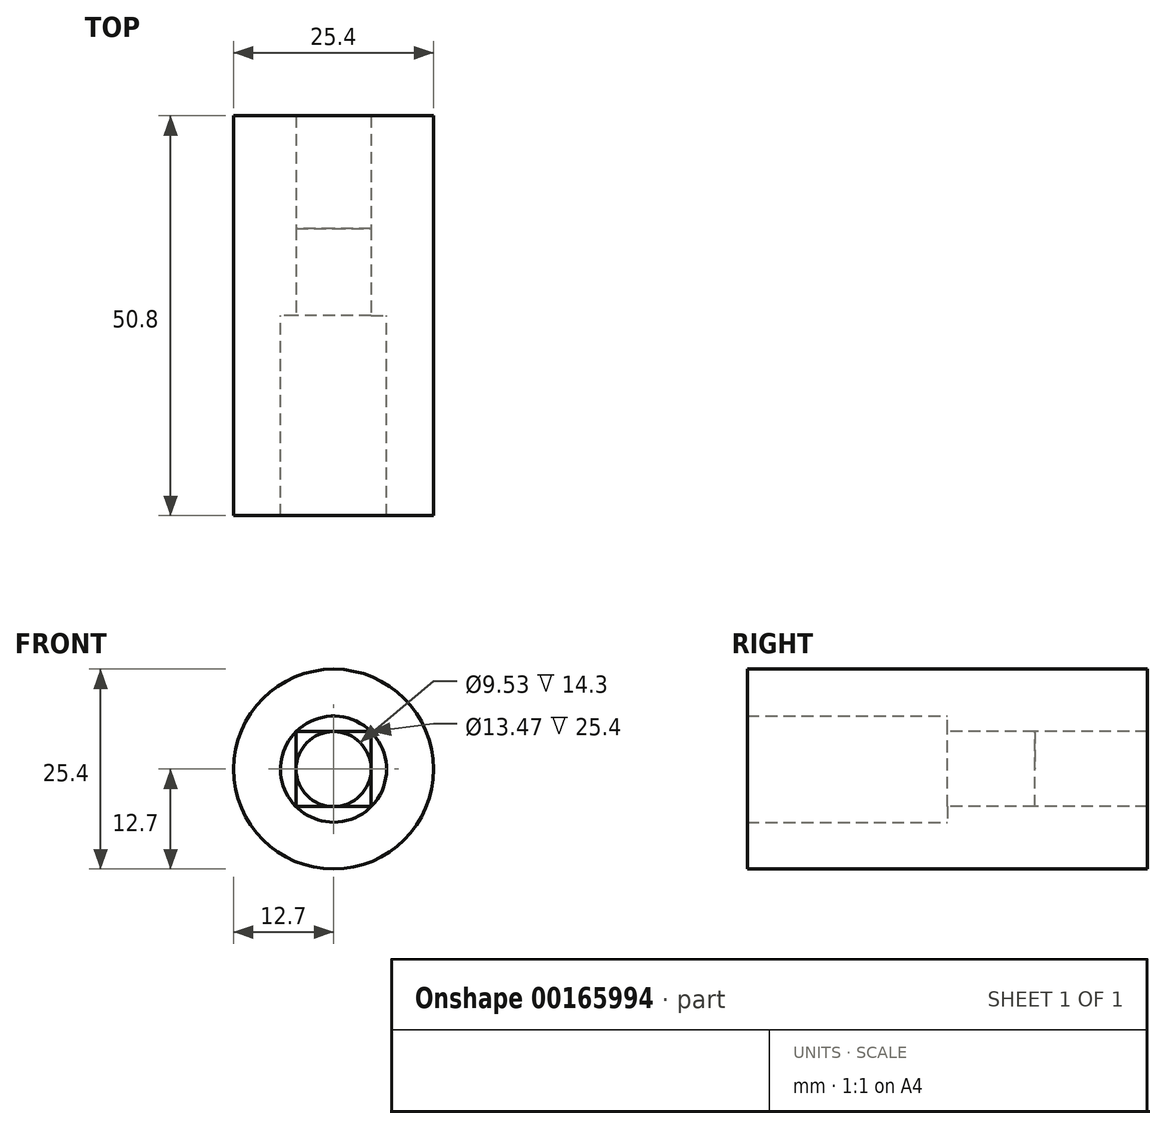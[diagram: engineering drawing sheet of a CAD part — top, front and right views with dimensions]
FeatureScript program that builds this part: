
annotation { "Feature Type Name" : "Feature", "Feature Type Description" : "" }
export const myFeature = defineFeature(function(context is Context, id is Id, definition is map)
    precondition{}
    {
        {
            var Q0;
            Q0=qCreatedBy(makeId("Front.planeOp"),FACE);
            var sketch = newSketch(context, id + "F0", { "sketchPlane" : qUnion([Q0])});
            skCircle(sketch, "E0", {"center": v(0, 0) * mm, "radius": 12.7 * mm});
            skSolve(sketch);
        }
        {
            var Q0;
            Q0 = qSketchRegion(id + "F0", true);
            extrude(context, id + "F1", {"entities" : qUnion([Q0]), "depth" : 25.4 * mm});
        }
        {
            var Q0;
            Q0=makeQuery(id+"F1.opExtrude","CAP_FACE",FACE,{"disambiguationData":[OSD([sQuery(id+"F0.wireOp",EDGE,"E0")])],"isStart":false});
            var sketch = newSketch(context, id + "F2", { "sketchPlane" : qUnion([Q0])});
            skLineSegment(sketch, "E1.bottom", {"start": v(4.76, -4.76) * mm, "end": v(-4.76, -4.76) * mm});
            skLineSegment(sketch, "E1.top", {"start": v(4.76, 4.76) * mm, "end": v(-4.76, 4.76) * mm});
            skLineSegment(sketch, "E1.left", {"start": v(4.76, -4.76) * mm, "end": v(4.76, 4.76) * mm});
            skLineSegment(sketch, "E1.right", {"start": v(-4.76, -4.76) * mm, "end": v(-4.76, 4.76) * mm});
            skPoint(sketch, "E1.middle", {"position": v(0, 0) * mm});
            skCircle(sketch, "E2", {"center": v(0, 0) * mm, "radius": 4.76 * mm});
            skSolve(sketch);
        }
        {
            var Q0;
            {var subQ0=sQuery(id+"F2.wireOp",EDGE,"E2");var subQ1=makeQuery(id+"F2.imprint","INTERSECT",VERTEX,{"derivedFrom":[sQuery(id+"F2.wireOp",EDGE,"E1.top"),subQ0]});Q0=makeQuery(id+"F2.imprint","IMPRINT",FACE,{"disambiguationData":[TD([[makeQuery(id+"F2.imprint","IMPRINT",EDGE,{"disambiguationData":[TD([[subQ1,1.0]])],"derivedFrom":subQ0}),1.0]])]});}
            extrude(context, id + "F3", {"entities" : qUnion([Q0]), "operationType" : NewBodyOperationType.REMOVE, "endBound" : BoundingType.THROUGH_ALL, "oppositeDirection" : true, "depth" : 25.4 * mm});
        }
        {
            var Q0;
            {var subQ0=sQuery(id+"F2.wireOp",EDGE,"E1.right");var subQ1=sQuery(id+"F2.wireOp",EDGE,"E1.top");var subQ2=makeQuery(id+"F2.imprint","INTERSECT",VERTEX,{"derivedFrom":[subQ1,subQ0]});Q0=makeQuery(id+"F2.imprint","IMPRINT",FACE,{"disambiguationData":[TD([[makeQuery(id+"F2.imprint","IMPRINT",EDGE,{"disambiguationData":[TD([[subQ2,1.0]])],"derivedFrom":subQ1}),1.0]])]});}
            var Q1;
            {var subQ0=sQuery(id+"F2.wireOp",EDGE,"E1.left");var subQ1=sQuery(id+"F2.wireOp",EDGE,"E1.top");var subQ2=makeQuery(id+"F2.imprint","INTERSECT",VERTEX,{"derivedFrom":[subQ1,subQ0]});Q1=makeQuery(id+"F2.imprint","IMPRINT",FACE,{"disambiguationData":[TD([[makeQuery(id+"F2.imprint","IMPRINT",EDGE,{"disambiguationData":[TD([[subQ2,-1.0]])],"derivedFrom":subQ1}),1.0]])]});}
            var Q2;
            {var subQ0=sQuery(id+"F2.wireOp",EDGE,"E1.left");var subQ1=sQuery(id+"F2.wireOp",EDGE,"E1.bottom");var subQ2=makeQuery(id+"F2.imprint","INTERSECT",VERTEX,{"derivedFrom":[subQ1,subQ0]});Q2=makeQuery(id+"F2.imprint","IMPRINT",FACE,{"disambiguationData":[TD([[makeQuery(id+"F2.imprint","IMPRINT",EDGE,{"disambiguationData":[TD([[subQ2,-1.0]])],"derivedFrom":subQ1}),-1.0]])]});}
            var Q3;
            {var subQ0=sQuery(id+"F2.wireOp",EDGE,"E1.right");var subQ1=sQuery(id+"F2.wireOp",EDGE,"E1.bottom");var subQ2=makeQuery(id+"F2.imprint","INTERSECT",VERTEX,{"derivedFrom":[subQ1,subQ0]});Q3=makeQuery(id+"F2.imprint","IMPRINT",FACE,{"disambiguationData":[TD([[makeQuery(id+"F2.imprint","IMPRINT",EDGE,{"disambiguationData":[TD([[subQ2,1.0]])],"derivedFrom":subQ1}),-1.0]])]});}
            var Q4;
            Q4=sQuery(id+"F2.wireOp",EDGE,"E1.bottom");
            var Q5;
            Q5=sQuery(id+"F2.wireOp",EDGE,"E1.right");
            var Q6;
            Q6=sQuery(id+"F2.wireOp",EDGE,"E1.top");
            var Q7;
            Q7=sQuery(id+"F2.wireOp",EDGE,"E1.left");
            extrude(context, id + "F4", {"entities" : qUnion([Q0, Q1, Q2, Q3]), "operationType" : NewBodyOperationType.REMOVE, "surfaceEntities" : qUnion([Q4, Q5, Q6, Q7]), "oppositeDirection" : true, "depth" : 11.1 * mm});
        }
        {
            var Q0;
            Q0=makeQuery(id+"F1.opExtrude","CAP_FACE",FACE,{"disambiguationData":[OSD([sQuery(id+"F0.wireOp",EDGE,"E0")])],"isStart":false});
            var sketch = newSketch(context, id + "F5", { "sketchPlane" : qUnion([Q0])});
            skCircle(sketch, "E3", {"center": v(0, 0) * mm, "radius": 6.74 * mm});
            skCircle(sketch, "E4", {"center": v(0, 0) * mm, "radius": 12.87 * mm});
            skSolve(sketch);
        }
        {
            var Q0;
            Q0=makeQuery(id+"F5.imprint","IMPRINT",FACE,{"disambiguationData":[TD([[makeQuery(id+"F5.imprint","IMPRINT",EDGE,{"derivedFrom":makeQuery(id+"F1.opExtrude","CAP_EDGE",EDGE,{"disambiguationData":[OSD([sQuery(id+"F0.wireOp",EDGE,"E0")])],"isStart":false})}),1.0]])]});
            extrude(context, id + "F6", {"entities" : qUnion([Q0]), "operationType" : NewBodyOperationType.ADD, "depth" : 25.4 * mm});
        }
    });
